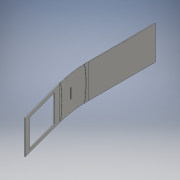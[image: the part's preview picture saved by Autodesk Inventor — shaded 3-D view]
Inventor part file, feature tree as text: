
AUTODESK INVENTOR PART (.ipt)
format: ipt  version: 2016 (Build 200138000, 138)  size: 208,384 bytes
history: native  units: mm
features: other x6, sketch x5, sheet_metal_op x3, reference x3
ambient origin geometry x8: Origin, YZ Plane, XZ Plane, XY Plane, X Axis, Y Axis, Z Axis, Center Point
bodies: Solid1 (feature_tree)
feature tree (17):
  sheet_metal_op  "Contour Flange1"
  sketch  "Sketch1"  dims[d2=5.0mm]
  reference  "Reference1"
  reference  "Reference2"
  reference  "Reference3"
  other  "Plate1"
  sheet_metal_op  "Bend1"
  sheet_metal_op  "Corner1"
  sketch  "Sketch2"  dims[d3=2.5mm]
  sketch  "Sketch4"  dims[d4=10.0mm]
  sketch  "Sketch5"  dims[d5=5.0mm]
  sketch  "Sketch6"  dims[d6=318.0mm d7=5.0mm d8=0.5mm d9=20.0mm d10=5.0mm d11=5.0mm d12=5.0mm d13=256.0mm d14=335.0mm d15=5.0mm d16=0.0mm d18=95.0mm d19=10.0mm d20=180.0mm d21=5.0mm d22=0.0mm d23=5.0mm d24=5.0mm d25=0.0mm d26=930.0mm d27=930.0mm d28=950.0mm d29=1216.0mm d30=2.0mm d31=2.0mm d32=5.0mm d33=0.0mm d34=223.0mm]
  other  "Cut1"
  other  "Cut2"
  other  "Cut3"
  other  "Cut4"
  other  "Definition1"
